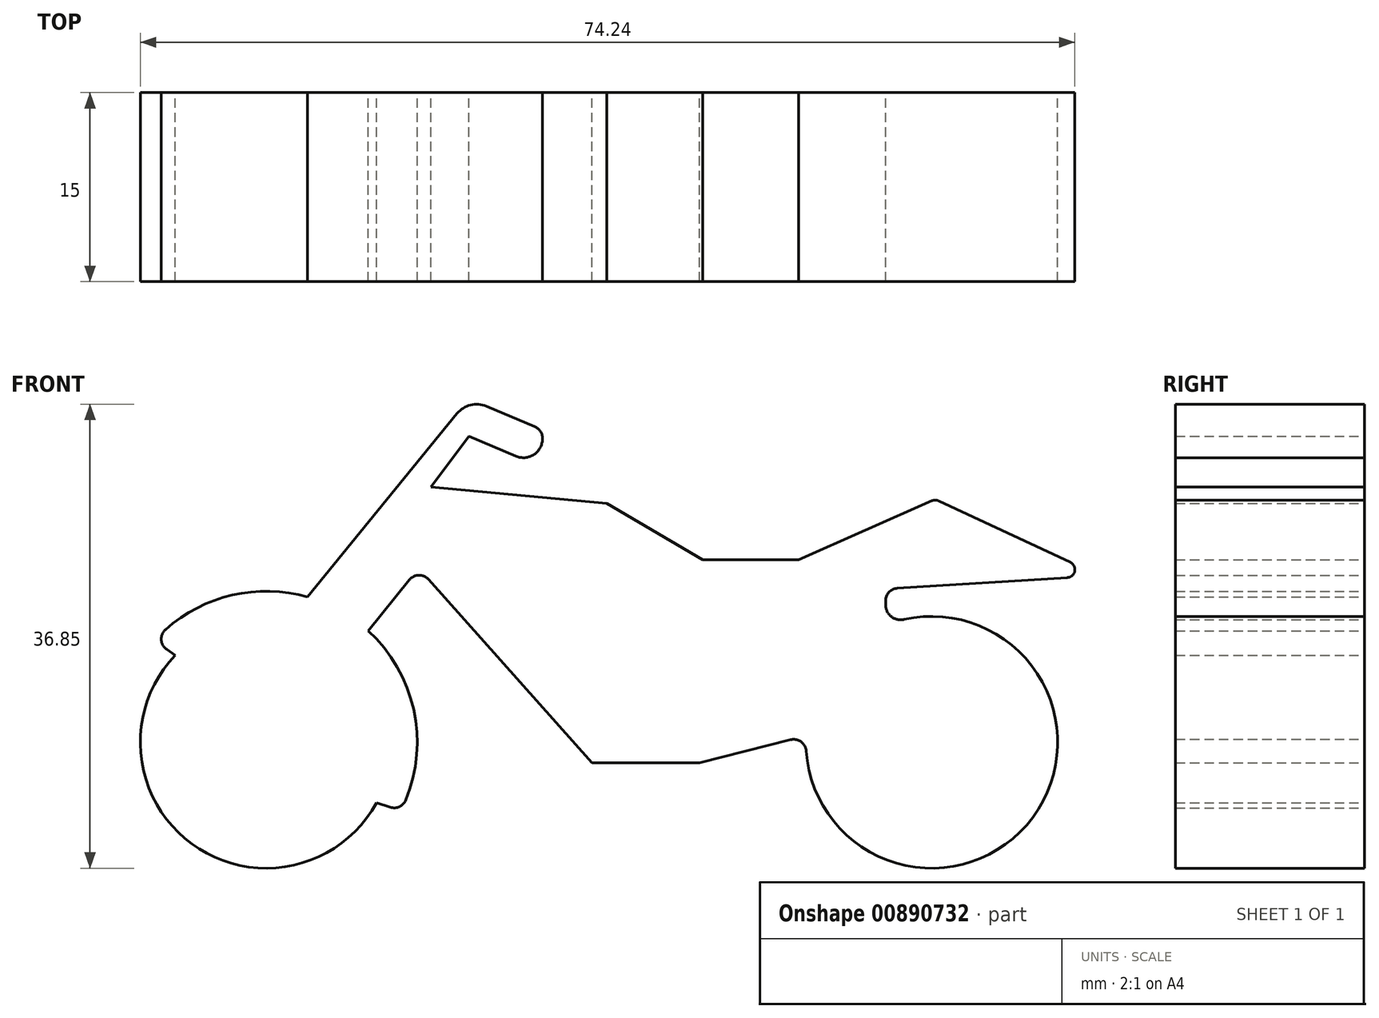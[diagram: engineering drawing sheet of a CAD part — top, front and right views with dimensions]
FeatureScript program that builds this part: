
annotation { "Feature Type Name" : "Feature", "Feature Type Description" : "" }
export const myFeature = defineFeature(function(context is Context, id is Id, definition is map)
    precondition{}
    {
        {
            var Q0;
            Q0=qCreatedBy(makeId("Front.planeOp"),FACE);
            var sketch = newSketch(context, id + "F0", { "sketchPlane" : qUnion([Q0])});
            skArc(sketch, "E0", {"start": v(-49.54, 6.9) * mm, "mid": v(-48.22, -8.07) * mm, "end": v(-33.54, -4.81) * mm});
            skArc(sketch, "E1", {"start": v(0.6, -0.7) * mm, "mid": v(18.6, -5.97) * mm, "end": v(8.37, 9.75) * mm});
            skLineSegment(sketch, "E2", {"start": v(-39.01, 11.54) * mm, "end": v(-27.14, 26.12) * mm});
            skLineSegment(sketch, "E3", {"start": v(-24.8, 26.7) * mm, "end": v(-20.96, 25.07) * mm});
            skLineSegment(sketch, "E4", {"start": v(-26.2, 24.3) * mm, "end": v(-29.23, 20.27) * mm});
            skLineSegment(sketch, "E5", {"start": v(-29.23, 20.27) * mm, "end": v(-15.24, 18.98) * mm});
            skLineSegment(sketch, "E6", {"start": v(-15.24, 18.98) * mm, "end": v(-7.63, 14.5) * mm});
            skLineSegment(sketch, "E7", {"start": v(11.14, 19.18) * mm, "end": v(21.58, 14.3) * mm});
            skLineSegment(sketch, "E8", {"start": v(21.35, 13.08) * mm, "end": v(7.85, 12.24) * mm});
            skLineSegment(sketch, "E9", {"start": v(6.9, 11.24) * mm, "end": v(6.9, 10.93) * mm});
            skLineSegment(sketch, "E10", {"start": v(-34.21, 8.86) * mm, "end": v(-30.92, 12.9) * mm});
            skLineSegment(sketch, "E11", {"start": v(-29.4, 12.94) * mm, "end": v(-16.41, -1.62) * mm});
            skLineSegment(sketch, "E12", {"start": v(-16.41, -1.62) * mm, "end": v(-7.87, -1.62) * mm});
            skLineSegment(sketch, "E13", {"start": v(-7.87, -1.62) * mm, "end": v(-0.64, 0.2) * mm});
            skArc(sketch, "E14.0", {"start": v(-38.96, 11.52) * mm, "mid": v(-44.96, 11.7) * mm, "end": v(-50.3, 8.94) * mm});
            skLineSegment(sketch, "E15", {"start": v(-50.21, 7.38) * mm, "end": v(-49.54, 6.9) * mm});
            skLineSegment(sketch, "E16", {"start": v(-33.54, -4.81) * mm, "end": v(-32.44, -5.16) * mm});
            skArc(sketch, "E17.trimOffspring", {"start": v(-31.22, -4.6) * mm, "mid": v(-30.6, 2.62) * mm, "end": v(-34.23, 8.88) * mm});
            skLineSegment(sketch, "E18", {"start": v(-26.2, 24.3) * mm, "end": v(-22.44, 22.72) * mm});
            skLineSegment(sketch, "E19", {"start": v(-20.36, 23.99) * mm, "end": v(-20.36, 24.07) * mm});
            skLineSegment(sketch, "E20", {"start": v(-7.9, 14.5) * mm, "end": v(0, 14.5) * mm});
            skLineSegment(sketch, "E21", {"start": v(0, 14.5) * mm, "end": v(10.61, 19.18) * mm});
            skPoint(sketch, "E22.visualSharp", {"position": v(23.84, 13.24) * mm});
            skArc(sketch, "E22.filletArc", {"start": v(21.35, 13.08) * mm, "mid": v(21.93, 13.6) * mm, "end": v(21.58, 14.3) * mm});
            skPoint(sketch, "E23.visualSharp", {"position": v(10.88, 19.3) * mm});
            skArc(sketch, "E23.filletArc", {"start": v(11.14, 19.18) * mm, "mid": v(10.88, 19.24) * mm, "end": v(10.61, 19.18) * mm});
            skPoint(sketch, "E24.visualSharp", {"position": v(-30.18, 13.82) * mm});
            skArc(sketch, "E24.filletArc", {"start": v(-29.4, 12.94) * mm, "mid": v(-30.17, 13.27) * mm, "end": v(-30.92, 12.9) * mm});
            skPoint(sketch, "E25.visualSharp", {"position": v(-26.2, 27.28) * mm});
            skArc(sketch, "E25.filletArc", {"start": v(-24.8, 26.7) * mm, "mid": v(-26.07, 26.8) * mm, "end": v(-27.14, 26.12) * mm});
            skPoint(sketch, "E26.visualSharp", {"position": v(-20.3, 24.8) * mm});
            skArc(sketch, "E26.filletArc", {"start": v(-20.36, 24.07) * mm, "mid": v(-20.5, 24.67) * mm, "end": v(-20.96, 25.07) * mm});
            skPoint(sketch, "E27.visualSharp", {"position": v(-20.52, 21.91) * mm});
            skArc(sketch, "E27.filletArc", {"start": v(-22.44, 22.72) * mm, "mid": v(-21.08, 22.82) * mm, "end": v(-20.36, 23.99) * mm});
            skPoint(sketch, "E28.visualSharp", {"position": v(-51.2, 8.06) * mm});
            skArc(sketch, "E28.filletArc", {"start": v(-50.3, 8.94) * mm, "mid": v(-50.64, 8.14) * mm, "end": v(-50.21, 7.38) * mm});
            skPoint(sketch, "E29.visualSharp", {"position": v(-31.6, -5.43) * mm});
            skArc(sketch, "E29.filletArc", {"start": v(-32.44, -5.16) * mm, "mid": v(-31.72, -5.12) * mm, "end": v(-31.22, -4.6) * mm});
            skPoint(sketch, "E30.visualSharp", {"position": v(6.9, 12.18) * mm});
            skArc(sketch, "E30.filletArc", {"start": v(7.85, 12.24) * mm, "mid": v(7.18, 11.92) * mm, "end": v(6.9, 11.24) * mm});
            skPoint(sketch, "E31.visualSharp", {"position": v(6.9, 9.3) * mm});
            skArc(sketch, "E31.filletArc", {"start": v(6.9, 10.93) * mm, "mid": v(7.36, 9.99) * mm, "end": v(8.37, 9.75) * mm});
            skPoint(sketch, "E32.visualSharp", {"position": v(0.59, 0.51) * mm});
            skArc(sketch, "E32.filletArc", {"start": v(0.6, -0.7) * mm, "mid": v(0.19, 0.04) * mm, "end": v(-0.64, 0.2) * mm});
            skSolve(sketch);
        }
        {
            var Q0;
            Q0=makeQuery(id+"F0.imprint","IMPRINT",FACE,{"disambiguationData":[TD([[makeQuery(id+"F0.imprint","IMPRINT",EDGE,{"derivedFrom":sQuery(id+"F0.wireOp",EDGE,"E0")}),1.0]])]});
            extrude(context, id + "F1", {"entities" : qUnion([Q0]), "depth" : 15 * mm, "offsetDistance" : 25 * mm});
        }
    });
